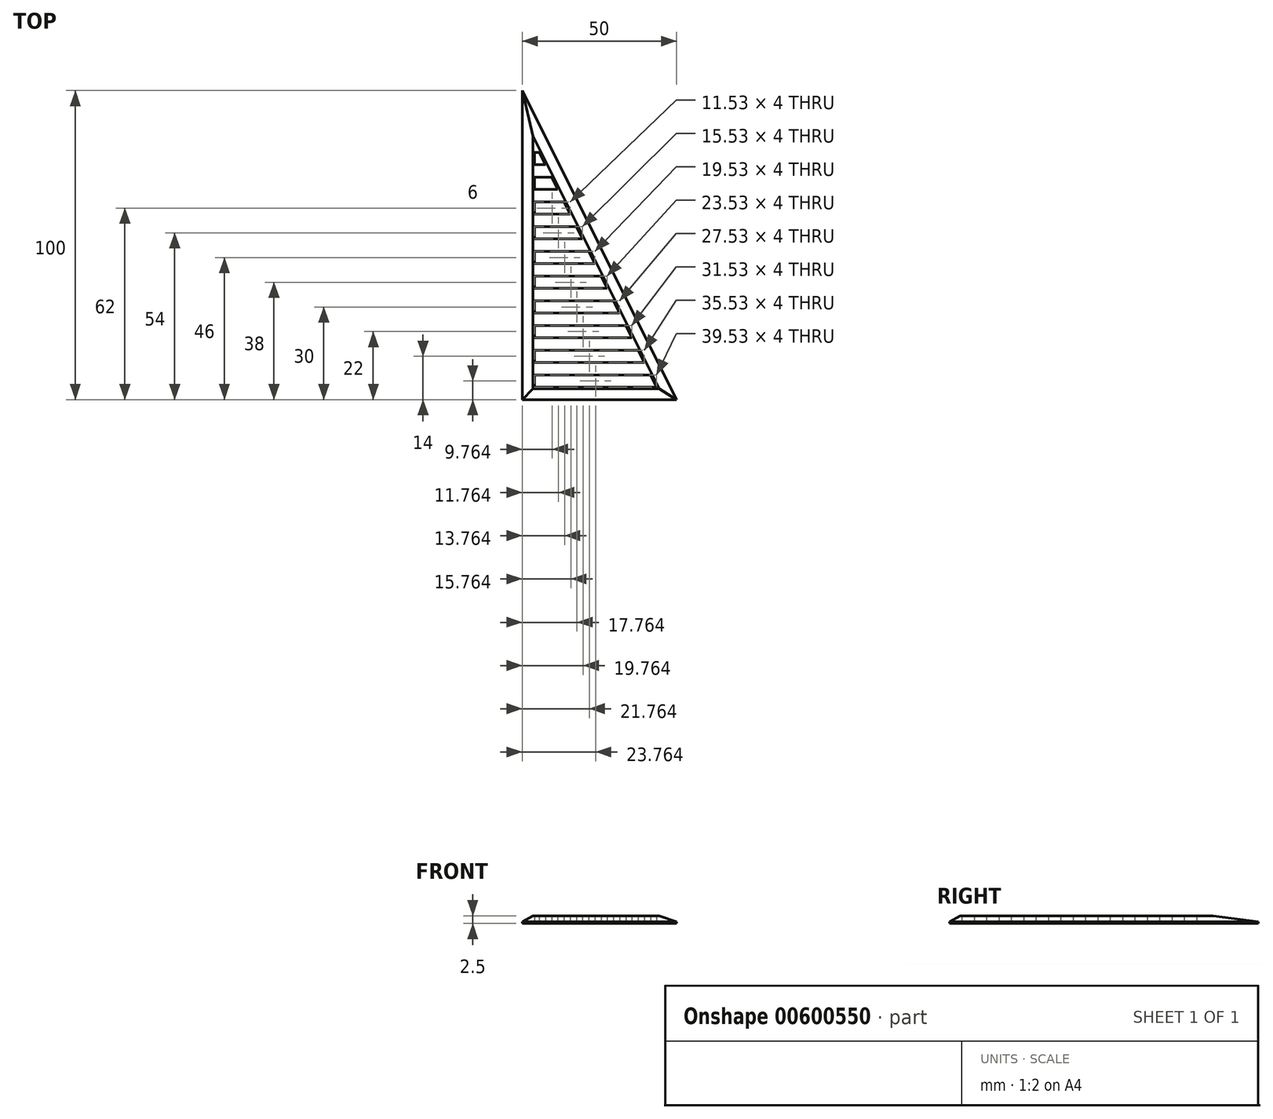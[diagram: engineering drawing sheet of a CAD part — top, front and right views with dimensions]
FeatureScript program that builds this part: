
annotation { "Feature Type Name" : "Feature", "Feature Type Description" : "" }
export const myFeature = defineFeature(function(context is Context, id is Id, definition is map)
    precondition{}
    {
        {
            var Q0;
            Q0=qCreatedBy(makeId("Top.planeOp"),FACE);
            var sketch = newSketch(context, id + "F0", { "sketchPlane" : qUnion([Q0])});
            skLineSegment(sketch, "E0", {"start": v(0, 0) * mm, "end": v(0, 100) * mm});
            skLineSegment(sketch, "E1", {"start": v(0, 0) * mm, "end": v(50, 0) * mm});
            skLineSegment(sketch, "E2", {"start": v(0, 100) * mm, "end": v(50, 0) * mm});
            skLineSegment(sketch, "E3.bottom", {"start": v(4, 4) * mm, "end": v(43.53, 4) * mm});
            skLineSegment(sketch, "E3.top", {"start": v(4, 8) * mm, "end": v(41.53, 8) * mm});
            skLineSegment(sketch, "E3.left", {"start": v(4, 4) * mm, "end": v(4, 8) * mm});
            skLineSegment(sketch, "E4.0", {"start": v(5.53, 80) * mm, "end": v(7.53, 76) * mm});
            skLineSegment(sketch, "E5.0.1.0", {"start": v(4, 16) * mm, "end": v(37.53, 16) * mm});
            skLineSegment(sketch, "E5.0.1.1", {"start": v(4, 12) * mm, "end": v(39.53, 12) * mm});
            skLineSegment(sketch, "E5.0.1.2", {"start": v(4, 12) * mm, "end": v(4, 16) * mm});
            skLineSegment(sketch, "E5.0.2.0", {"start": v(4, 24) * mm, "end": v(33.53, 24) * mm});
            skLineSegment(sketch, "E5.0.2.1", {"start": v(4, 20) * mm, "end": v(35.53, 20) * mm});
            skLineSegment(sketch, "E5.0.2.2", {"start": v(4, 20) * mm, "end": v(4, 24) * mm});
            skLineSegment(sketch, "E5.0.3.0", {"start": v(4, 32) * mm, "end": v(29.53, 32) * mm});
            skLineSegment(sketch, "E5.0.3.1", {"start": v(4, 28) * mm, "end": v(31.53, 28) * mm});
            skLineSegment(sketch, "E5.0.3.2", {"start": v(4, 28) * mm, "end": v(4, 32) * mm});
            skLineSegment(sketch, "E5.0.4.0", {"start": v(4, 40) * mm, "end": v(25.53, 40) * mm});
            skLineSegment(sketch, "E5.0.4.1", {"start": v(4, 36) * mm, "end": v(27.53, 36) * mm});
            skLineSegment(sketch, "E5.0.4.2", {"start": v(4, 36) * mm, "end": v(4, 40) * mm});
            skLineSegment(sketch, "E5.0.5.0", {"start": v(4, 48) * mm, "end": v(21.53, 48) * mm});
            skLineSegment(sketch, "E5.0.5.1", {"start": v(4, 44) * mm, "end": v(23.53, 44) * mm});
            skLineSegment(sketch, "E5.0.5.2", {"start": v(4, 44) * mm, "end": v(4, 48) * mm});
            skLineSegment(sketch, "E5.0.6.0", {"start": v(4, 56) * mm, "end": v(17.53, 56) * mm});
            skLineSegment(sketch, "E5.0.6.1", {"start": v(4, 52) * mm, "end": v(19.53, 52) * mm});
            skLineSegment(sketch, "E5.0.6.2", {"start": v(4, 52) * mm, "end": v(4, 56) * mm});
            skLineSegment(sketch, "E5.0.7.0", {"start": v(4, 64) * mm, "end": v(13.53, 64) * mm});
            skLineSegment(sketch, "E5.0.7.1", {"start": v(4, 60) * mm, "end": v(15.53, 60) * mm});
            skLineSegment(sketch, "E5.0.7.2", {"start": v(4, 60) * mm, "end": v(4, 64) * mm});
            skLineSegment(sketch, "E5.0.8.0", {"start": v(4, 72) * mm, "end": v(9.53, 72) * mm});
            skLineSegment(sketch, "E5.0.8.1", {"start": v(4, 68) * mm, "end": v(11.53, 68) * mm});
            skLineSegment(sketch, "E5.0.8.2", {"start": v(4, 68) * mm, "end": v(4, 72) * mm});
            skLineSegment(sketch, "E5.0.9.0", {"start": v(4, 80) * mm, "end": v(5.53, 80) * mm});
            skLineSegment(sketch, "E5.0.9.1", {"start": v(4, 76) * mm, "end": v(7.53, 76) * mm});
            skLineSegment(sketch, "E5.0.9.2", {"start": v(4, 76) * mm, "end": v(4, 80) * mm});
            skLineSegment(sketch, "E5.direction1", {"start": v(4, 4) * mm, "end": v(29, 4) * mm, "construction": true});
            skLineSegment(sketch, "E5.direction2", {"start": v(4, 4) * mm, "end": v(4, 12) * mm, "construction": true});
            skPoint(sketch, "E6.orphan", {"position": v(60.04, 80) * mm});
            skPoint(sketch, "E7.orphan", {"position": v(60.04, 76) * mm});
            skPoint(sketch, "E8.orphan", {"position": v(60.04, 72) * mm});
            skPoint(sketch, "E9.orphan", {"position": v(60.04, 68) * mm});
            skPoint(sketch, "E10.orphan", {"position": v(60.04, 52) * mm});
            skPoint(sketch, "E11.orphan", {"position": v(60.04, 56) * mm});
            skPoint(sketch, "E12.orphan", {"position": v(60.04, 60) * mm});
            skPoint(sketch, "E13.orphan", {"position": v(60.04, 64) * mm});
            skPoint(sketch, "E14.orphan", {"position": v(60.04, 12) * mm});
            skPoint(sketch, "E15.orphan", {"position": v(60.04, 16) * mm});
            skPoint(sketch, "E16.orphan", {"position": v(60.04, 20) * mm});
            skPoint(sketch, "E17.orphan", {"position": v(60.04, 24) * mm});
            skPoint(sketch, "E18.orphan", {"position": v(60.04, 28) * mm});
            skPoint(sketch, "E19.orphan", {"position": v(60.04, 32) * mm});
            skPoint(sketch, "E20.orphan", {"position": v(60.04, 36) * mm});
            skPoint(sketch, "E21.orphan", {"position": v(60.04, 40) * mm});
            skPoint(sketch, "E22.orphan", {"position": v(60.04, 48) * mm});
            skLineSegment(sketch, "E23.trimOffspring", {"start": v(41.53, 8) * mm, "end": v(43.53, 4) * mm});
            skLineSegment(sketch, "E24.trimOffspring", {"start": v(37.53, 16) * mm, "end": v(39.53, 12) * mm});
            skLineSegment(sketch, "E25.trimOffspring", {"start": v(33.53, 24) * mm, "end": v(35.53, 20) * mm});
            skLineSegment(sketch, "E26.trimOffspring", {"start": v(29.53, 32) * mm, "end": v(31.53, 28) * mm});
            skLineSegment(sketch, "E27.trimOffspring", {"start": v(25.53, 40) * mm, "end": v(27.53, 36) * mm});
            skLineSegment(sketch, "E28.trimOffspring", {"start": v(21.53, 48) * mm, "end": v(23.53, 44) * mm});
            skLineSegment(sketch, "E29.trimOffspring", {"start": v(17.53, 56) * mm, "end": v(19.53, 52) * mm});
            skLineSegment(sketch, "E30.trimOffspring", {"start": v(13.53, 64) * mm, "end": v(15.53, 60) * mm});
            skLineSegment(sketch, "E31.trimOffspring", {"start": v(9.53, 72) * mm, "end": v(11.53, 68) * mm});
            skSolve(sketch);
        }
        {
            var Q0;
            Q0=makeQuery(id+"F0.imprint","IMPRINT",FACE,{"disambiguationData":[TD([[makeQuery(id+"F0.imprint","IMPRINT",EDGE,{"derivedFrom":sQuery(id+"F0.wireOp",EDGE,"E0")}),-1.0]])]});
            extrude(context, id + "F1", {"entities" : qUnion([Q0]), "depth" : 2.5 * mm, "offsetDistance" : 25 * mm});
        }
        {
            var Q0;
            Q0=makeQuery(id+"F1.opExtrude","CAP_EDGE",EDGE,{"disambiguationData":[OSD([sQuery(id+"F0.wireOp",EDGE,"E0")])],"isStart":false});
            var Q1;
            Q1=makeQuery(id+"F1.opExtrude","CAP_EDGE",EDGE,{"disambiguationData":[OSD([sQuery(id+"F0.wireOp",EDGE,"E2")])],"isStart":false});
            var Q2;
            Q2=makeQuery(id+"F1.opExtrude","CAP_EDGE",EDGE,{"disambiguationData":[OSD([sQuery(id+"F0.wireOp",EDGE,"E1")])],"isStart":false});
            chamfer(context, id + "F2", {"entities" : qUnion([Q0, Q1, Q2]), "chamferType" : ChamferType.OFFSET_ANGLE, "width" : 2 * mm, "oppositeDirection" : false, "angle" : 60 * degree, "tangentPropagation" : true});
        }
    });
